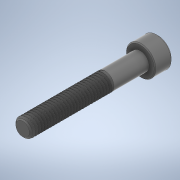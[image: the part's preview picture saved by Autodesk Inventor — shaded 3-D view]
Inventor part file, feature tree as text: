
AUTODESK INVENTOR PART (.ipt)
format: ipt  version: 2020 (Build 240168000, 168)  size: 836,096 bytes
history: native  units: in
note: dims shown in document units (in); Inventor stores cm internally (conversion verified against a paired STEP export)
features: chamfer x1
ambient origin geometry x8: Origin, YZ Plane, XZ Plane, XY Plane, X Axis, Y Axis, Z Axis, Center Point
bodies: Solid1 (feature_tree)
feature tree (1):
  chamfer  "Chamfer2"  [1 undecoded]
note: 1 required parameter value undecoded (feature->parameter linkage not recoverable at this tier; creation-order binding heuristic only, values carry confidence <= 0.55)
